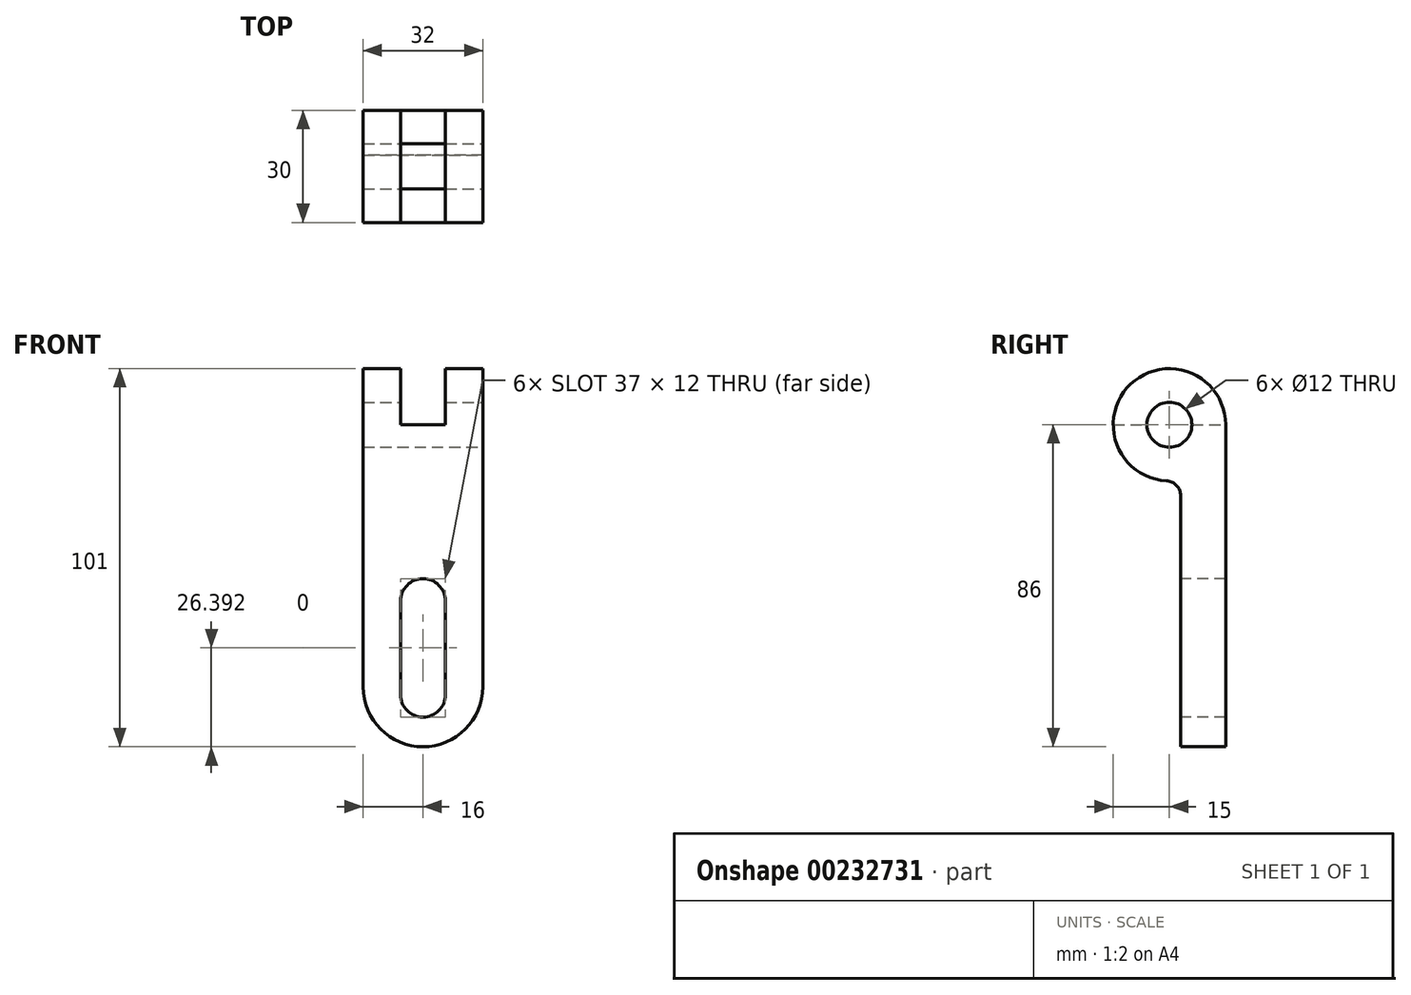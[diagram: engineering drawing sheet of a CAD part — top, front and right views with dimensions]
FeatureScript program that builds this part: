
annotation { "Feature Type Name" : "Feature", "Feature Type Description" : "" }
export const myFeature = defineFeature(function(context is Context, id is Id, definition is map)
    precondition{}
    {
        {
            var Q0;
            Q0=qCreatedBy(makeId("Right.planeOp"),FACE);
            var sketch = newSketch(context, id + "F0", { "sketchPlane" : qUnion([Q0])});
            skCircle(sketch, "E0", {"center": v(0, 0) * mm, "radius": 6 * mm});
            skArc(sketch, "E1", {"start": v(15, 0) * mm, "mid": v(-10.32, 10.88) * mm, "end": v(-0.79, -14.98) * mm});
            skLineSegment(sketch, "E2", {"start": v(15, 0) * mm, "end": v(15, -86) * mm});
            skLineSegment(sketch, "E3", {"start": v(15, -86) * mm, "end": v(3, -86) * mm});
            skLineSegment(sketch, "E4", {"start": v(3, -86) * mm, "end": v(3, -18.97) * mm});
            skPoint(sketch, "E5.visualSharp", {"position": v(3, -14.7) * mm});
            skArc(sketch, "E5.filletArc", {"start": v(3, -18.97) * mm, "mid": v(1.9, -16.22) * mm, "end": v(-0.79, -14.98) * mm});
            skSolve(sketch);
        }
        {
            var Q0;
            Q0=makeQuery(id+"F0.imprint","IMPRINT",FACE,{"disambiguationData":[TD([[makeQuery(id+"F0.imprint","IMPRINT",EDGE,{"derivedFrom":sQuery(id+"F0.wireOp",EDGE,"E0")}),-1.0]])]});
            var Q1;
            Q1 = qSketchRegion(id + "F2", true);
            extrude(context, id + "F1", {"entities" : qUnion([Q0, Q1]), "oppositeDirection" : true, "depth" : 32 * mm});
        }
        {
            var Q0;
            Q0=qCreatedBy(makeId("Front.planeOp"),FACE);
            var sketch = newSketch(context, id + "F2", { "sketchPlane" : qUnion([Q0])});
            skLineSegment(sketch, "E6.0.0", {"start": v(0, -86) * mm, "end": v(0, -70) * mm, "construction": true});
            skLineSegment(sketch, "E6.0.1", {"start": v(0, -18.97) * mm, "end": v(-32, -18.97) * mm, "construction": true});
            skLineSegment(sketch, "E6.0.2", {"start": v(-32, -18.97) * mm, "end": v(-32, -58.76) * mm, "construction": true});
            skLineSegment(sketch, "E6.0.3", {"start": v(-32, -86) * mm, "end": v(0, -86) * mm, "construction": true});
            skLineSegment(sketch, "E7", {"start": v(-16, 15) * mm, "end": v(-16, -86) * mm, "construction": true});
            skLineSegment(sketch, "E8", {"start": v(-32, 15) * mm, "end": v(0, 15) * mm, "construction": true});
            skArc(sketch, "E9", {"start": v(-32, -70) * mm, "mid": v(-16, -86) * mm, "end": v(0, -70) * mm});
            skLineSegment(sketch, "E10", {"start": v(-32, -70) * mm, "end": v(-32, -86) * mm});
            skLineSegment(sketch, "E11", {"start": v(0, -86) * mm, "end": v(0, -70) * mm});
            skLineSegment(sketch, "E12.trimOffspring", {"start": v(-32, -70) * mm, "end": v(-32, -86) * mm, "construction": true});
            skLineSegment(sketch, "E13.trimOffspring", {"start": v(0, -54.86) * mm, "end": v(0, -18.97) * mm, "construction": true});
            skPoint(sketch, "E14", {"position": v(-16, -86) * mm});
            skLineSegment(sketch, "E15", {"start": v(-10, -47.1) * mm, "end": v(-10, -72.1) * mm});
            skLineSegment(sketch, "E16", {"start": v(-22, -47.1) * mm, "end": v(-22, -72.1) * mm});
            skArc(sketch, "E17", {"start": v(-22, -72.1) * mm, "mid": v(-16, -78.1) * mm, "end": v(-10, -72.1) * mm});
            skArc(sketch, "E18", {"start": v(-10, -47.1) * mm, "mid": v(-16, -41.1) * mm, "end": v(-22, -47.1) * mm});
            skLineSegment(sketch, "E19", {"start": v(0, -86) * mm, "end": v(-16, -86) * mm});
            skLineSegment(sketch, "E20", {"start": v(-16, -86) * mm, "end": v(-32, -86) * mm});
            skSolve(sketch);
        }
        {
            var Q0;
            {var subQ0=sQuery(id+"F2.wireOp",EDGE,"E10");Q0=makeQuery(id+"F2.imprint","IMPRINT",FACE,{"disambiguationData":[TD([[makeQuery(id+"F2.imprint","IMPRINT",EDGE,{"derivedFrom":subQ0}),1.0]])]});}
            var Q1;
            {var subQ0=sQuery(id+"F2.wireOp",EDGE,"E11");Q1=makeQuery(id+"F2.imprint","IMPRINT",FACE,{"disambiguationData":[TD([[makeQuery(id+"F2.imprint","IMPRINT",EDGE,{"derivedFrom":subQ0}),1.0]])]});}
            var Q2;
            Q2=makeQuery(id+"F2.imprint","IMPRINT",FACE,{"disambiguationData":[TD([[makeQuery(id+"F2.imprint","IMPRINT",EDGE,{"derivedFrom":sQuery(id+"F2.wireOp",EDGE,"E15")}),-1.0]])]});
            extrude(context, id + "F3", {"entities" : qUnion([Q0, Q1, Q2]), "operationType" : NewBodyOperationType.REMOVE, "endBound" : BoundingType.THROUGH_ALL, "oppositeDirection" : true, "depth" : 25 * mm});
        }
        {
            var Q0;
            Q0=makeQuery(id+"F1.opExtrude","SWEPT_FACE",FACE,{"disambiguationData":[OSD([sQuery(id+"F0.wireOp",EDGE,"E2")])]});
            var sketch = newSketch(context, id + "F4", { "sketchPlane" : qUnion([Q0])});
            skArc(sketch, "E21.0.0", {"start": v(0, -70) * mm, "mid": v(16, -86) * mm, "end": v(32, -70) * mm, "construction": true});
            skLineSegment(sketch, "E21.0.1", {"start": v(32, -70) * mm, "end": v(32, 0) * mm, "construction": true});
            skLineSegment(sketch, "E21.0.2", {"start": v(32, 0) * mm, "end": v(0, 0) * mm, "construction": true});
            skLineSegment(sketch, "E21.0.3", {"start": v(0, 0) * mm, "end": v(0, -70) * mm, "construction": true});
            skLineSegment(sketch, "E22", {"start": v(10, 15) * mm, "end": v(22, 15) * mm});
            skLineSegment(sketch, "E23", {"start": v(22, 15) * mm, "end": v(22, -25) * mm});
            skLineSegment(sketch, "E24", {"start": v(22, -25) * mm, "end": v(10, -25) * mm});
            skLineSegment(sketch, "E25", {"start": v(10, -25) * mm, "end": v(10, 15) * mm});
            skSolve(sketch);
        }
        {
            var Q0;
            {var subQ0=sQuery(id+"F4.wireOp",EDGE,"E22");Q0=makeQuery(id+"F4.imprint","IMPRINT",FACE,{"disambiguationData":[TD([[makeQuery(id+"F4.imprint","IMPRINT",EDGE,{"derivedFrom":subQ0}),-1.0]])]});}
            extrude(context, id + "F5", {"entities" : qUnion([Q0]), "operationType" : NewBodyOperationType.REMOVE, "endBound" : BoundingType.THROUGH_ALL, "oppositeDirection" : true, "depth" : 25 * mm});
        }
    });
